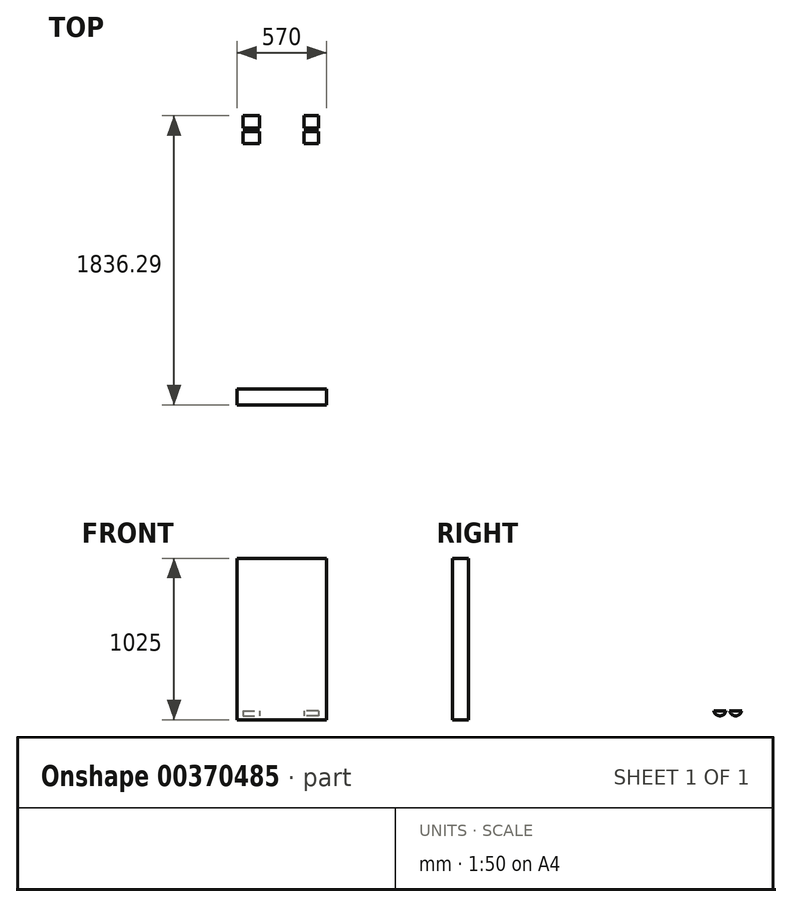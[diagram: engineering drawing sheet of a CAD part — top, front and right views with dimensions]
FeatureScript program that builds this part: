
annotation { "Feature Type Name" : "Feature", "Feature Type Description" : "" }
export const myFeature = defineFeature(function(context is Context, id is Id, definition is map)
    precondition{}
    {
        {
            var Q0;
            Q0=qCreatedBy(makeId("Top.planeOp"),FACE);
            var sketch = newSketch(context, id + "F0", { "sketchPlane" : qUnion([Q0])});
            skLineSegment(sketch, "E0", {"start": v(0, 0) * mm, "end": v(0, 799.3) * mm, "construction": true});
            skLineSegment(sketch, "E1", {"start": v(-100, 0) * mm, "end": v(-100, 2497.9) * mm});
            skLineSegment(sketch, "E2", {"start": v(-100.44, 2502.06) * mm, "end": v(-139.13, 2684.16) * mm});
            skLineSegment(sketch, "E3", {"start": v(-158.7, 2700) * mm, "end": v(-192.5, 2700) * mm});
            skLineSegment(sketch, "E4", {"start": v(-192.5, 2700) * mm, "end": v(-192.5, 0) * mm, "construction": true});
            skLineSegment(sketch, "E5", {"start": v(-192.5, 0) * mm, "end": v(-100, 0) * mm});
            skPoint(sketch, "E6.visualSharp", {"position": v(-142.5, 2700) * mm});
            skArc(sketch, "E6.filletArc", {"start": v(-139.13, 2684.16) * mm, "mid": v(-146.1, 2695.54) * mm, "end": v(-158.7, 2700) * mm});
            skPoint(sketch, "E7.visualSharp", {"position": v(-100, 2500) * mm});
            skArc(sketch, "E7.filletArc", {"start": v(-100, 2497.9) * mm, "mid": v(-100.1, 2499.99) * mm, "end": v(-100.44, 2502.06) * mm});
            skArc(sketch, "E8.MirrorCS", {"start": v(-285, 2497.9) * mm, "mid": v(-284.9, 2499.99) * mm, "end": v(-284.56, 2502.06) * mm});
            skLineSegment(sketch, "E9.MirrorCS", {"start": v(-226.3, 2700) * mm, "end": v(-192.5, 2700) * mm});
            skArc(sketch, "E10.MirrorCS", {"start": v(-245.87, 2684.16) * mm, "mid": v(-238.9, 2695.54) * mm, "end": v(-226.3, 2700) * mm});
            skLineSegment(sketch, "E11.MirrorCS", {"start": v(-192.5, 0) * mm, "end": v(-285, 0) * mm});
            skLineSegment(sketch, "E12.MirrorCS", {"start": v(-285, 0) * mm, "end": v(-285, 2497.9) * mm});
            skPoint(sketch, "E13.MirrorP", {"position": v(-285, 2500) * mm});
            skLineSegment(sketch, "E14.MirrorCS", {"start": v(-284.56, 2502.06) * mm, "end": v(-245.87, 2684.16) * mm});
            skPoint(sketch, "E15.MirrorP", {"position": v(-242.5, 2700) * mm});
            skArc(sketch, "E16.MirrorCS", {"start": v(100, 2497.9) * mm, "mid": v(100.1, 2499.99) * mm, "end": v(100.44, 2502.06) * mm});
            skArc(sketch, "E17.MirrorCS", {"start": v(285, 2497.9) * mm, "mid": v(284.9, 2499.99) * mm, "end": v(284.56, 2502.06) * mm});
            skLineSegment(sketch, "E18.MirrorCS", {"start": v(226.3, 2700) * mm, "end": v(192.5, 2700) * mm});
            skLineSegment(sketch, "E19.MirrorCS", {"start": v(158.7, 2700) * mm, "end": v(192.5, 2700) * mm});
            skArc(sketch, "E20.MirrorCS", {"start": v(245.87, 2684.16) * mm, "mid": v(238.9, 2695.54) * mm, "end": v(226.3, 2700) * mm});
            skArc(sketch, "E21.MirrorCS", {"start": v(139.13, 2684.16) * mm, "mid": v(146.1, 2695.54) * mm, "end": v(158.7, 2700) * mm});
            skLineSegment(sketch, "E22.MirrorCS", {"start": v(192.5, 0) * mm, "end": v(100, 0) * mm});
            skLineSegment(sketch, "E23.MirrorCS", {"start": v(192.5, 0) * mm, "end": v(285, 0) * mm});
            skPoint(sketch, "E24.MirrorP", {"position": v(242.5, 2700) * mm});
            skPoint(sketch, "E25.MirrorP", {"position": v(142.5, 2700) * mm});
            skLineSegment(sketch, "E26.MirrorCS", {"start": v(285, 0) * mm, "end": v(285, 2497.9) * mm});
            skLineSegment(sketch, "E27.MirrorCS", {"start": v(100, 0) * mm, "end": v(100, 2497.9) * mm});
            skPoint(sketch, "E28.MirrorP", {"position": v(285, 2500) * mm});
            skLineSegment(sketch, "E29.MirrorCS", {"start": v(284.56, 2502.06) * mm, "end": v(245.87, 2684.16) * mm});
            skPoint(sketch, "E30.MirrorP", {"position": v(100, 2500) * mm});
            skLineSegment(sketch, "E31.MirrorCS", {"start": v(100.44, 2502.06) * mm, "end": v(139.13, 2684.16) * mm});
            skLineSegment(sketch, "E32.MirrorCS", {"start": v(192.5, 2700) * mm, "end": v(192.5, 0) * mm, "construction": true});
            skLineSegment(sketch, "E33.bottom", {"start": v(-285, 0) * mm, "end": v(285, 0) * mm});
            skLineSegment(sketch, "E33.top", {"start": v(-285, -100) * mm, "end": v(285, -100) * mm});
            skLineSegment(sketch, "E33.left", {"start": v(-285, 0) * mm, "end": v(-285, -100) * mm});
            skLineSegment(sketch, "E33.right", {"start": v(285, 0) * mm, "end": v(285, -100) * mm});
            skSolve(sketch);
        }
        {
            var Q0;
            Q0=makeQuery(id+"F0.imprint","IMPRINT",FACE,{"disambiguationData":[TD([[makeQuery(id+"F0.imprint","IMPRINT",EDGE,{"derivedFrom":sQuery(id+"F0.wireOp",EDGE,"E8.MirrorCS")}),-1.0]])]});
            var Q1;
            Q1=makeQuery(id+"F0.imprint","IMPRINT",FACE,{"disambiguationData":[TD([[makeQuery(id+"F0.imprint","IMPRINT",EDGE,{"derivedFrom":sQuery(id+"F0.wireOp",EDGE,"E33.top")}),1.0]])]});
            var Q2;
            Q2=makeQuery(id+"F0.imprint","IMPRINT",FACE,{"disambiguationData":[TD([[makeQuery(id+"F0.imprint","IMPRINT",EDGE,{"derivedFrom":sQuery(id+"F0.wireOp",EDGE,"E16.MirrorCS")}),-1.0]])]});
            extrude(context, id + "F1", {"entities" : qUnion([Q0, Q1, Q2]), "depth" : 90 * mm, "hasSecondDirection" : true, "secondDirectionOppositeDirection" : false, "secondDirectionDepth" : 30 * mm});
        }
        {
            var Q0;
            Q0=makeQuery(id+"F0.imprint","IMPRINT",FACE,{"disambiguationData":[TD([[makeQuery(id+"F0.imprint","IMPRINT",EDGE,{"derivedFrom":sQuery(id+"F0.wireOp",EDGE,"E33.top")}),1.0]])]});
            extrude(context, id + "F2", {"entities" : qUnion([Q0]), "operationType" : NewBodyOperationType.ADD, "depth" : 1000 * mm, "hasSecondDirection" : true, "secondDirectionOppositeDirection" : true, "secondDirectionDepth" : 25 * mm});
        }
        {
            var Q0;
            Q0=qCreatedBy(makeId("Right.planeOp"),FACE);
            var sketch = newSketch(context, id + "F3", { "sketchPlane" : qUnion([Q0])});
            skArc(sketch, "E34", {"start": v(1558.83, 30) * mm, "mid": v(1597.56, 0) * mm, "end": v(1636.3, 30) * mm});
            skArc(sketch, "E35", {"start": v(1658.83, 30) * mm, "mid": v(1697.56, 0) * mm, "end": v(1736.3, 30) * mm});
            skLineSegment(sketch, "E36", {"start": v(1736.3, 30) * mm, "end": v(1658.83, 30) * mm});
            skLineSegment(sketch, "E37", {"start": v(1636.3, 30) * mm, "end": v(1558.83, 30) * mm});
            skSolve(sketch);
        }
        {
            var Q0;
            Q0=makeQuery(id+"F3.imprint","IMPRINT",FACE,{"disambiguationData":[TD([[makeQuery(id+"F3.imprint","IMPRINT",EDGE,{"derivedFrom":sQuery(id+"F3.wireOp",EDGE,"E35")}),1.0]])]});
            var Q1;
            Q1=makeQuery(id+"F3.imprint","IMPRINT",FACE,{"disambiguationData":[TD([[makeQuery(id+"F3.imprint","IMPRINT",EDGE,{"derivedFrom":sQuery(id+"F3.wireOp",EDGE,"E34")}),1.0]])]});
            extrude(context, id + "F4", {"entities" : qUnion([Q0, Q1]), "operationType" : NewBodyOperationType.ADD, "depth" : 233 * mm, "hasSecondDirection" : true, "secondDirectionOppositeDirection" : false, "secondDirectionDepth" : 141 * mm});
        }
        {
            var Q0;
            Q0 = qSketchRegion(id + "F3", true);
            extrude(context, id + "F5", {"entities" : qUnion([Q0]), "operationType" : NewBodyOperationType.ADD, "oppositeDirection" : true, "depth" : 247 * mm, "hasSecondDirection" : true, "secondDirectionOppositeDirection" : true, "secondDirectionDepth" : 142 * mm});
        }
        {
            var Q0;
            Q0=qCreatedBy(makeId("Right.planeOp"),FACE);
            var sketch = newSketch(context, id + "F6", { "sketchPlane" : qUnion([Q0])});
            skLineSegment(sketch, "E38", {"start": v(2700, 60) * mm, "end": v(2497.9, 30) * mm});
            skLineSegment(sketch, "E39", {"start": v(2497.9, 30) * mm, "end": v(2700, 30) * mm});
            skLineSegment(sketch, "E40", {"start": v(2700, 30) * mm, "end": v(2700, 60) * mm});
            skSolve(sketch);
        }
        {
            var Q0;
            Q0 = qSketchRegion(id + "F6", true);
            extrude(context, id + "F7", {"entities" : qUnion([Q0]), "operationType" : NewBodyOperationType.REMOVE, "endBound" : BoundingType.THROUGH_ALL, "oppositeDirection" : true, "depth" : 25 * mm, "hasSecondDirection" : true, "secondDirectionBound" : SecondDirectionBoundingType.THROUGH_ALL, "secondDirectionOppositeDirection" : false, "secondDirectionDepth" : 25 * mm});
        }
    });
